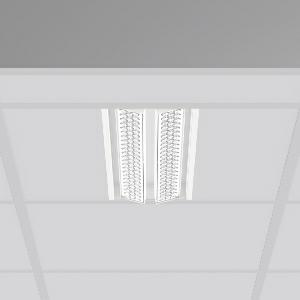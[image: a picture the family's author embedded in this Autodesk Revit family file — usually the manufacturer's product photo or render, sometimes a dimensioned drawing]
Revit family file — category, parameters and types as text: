
# Revit family: tx-move_901734_002_3_e3f6
name_source: partatom
category: Lighting Fixtures
units: mm (PartAtom-declared; Revit-internal decimal feet)

## family parameters
Cut with Voids When Loaded = No
Host = Face
Light Source = No
Part Type = Normal
Room Calculation Point = No
Round Connector Dimension = Use Diameter
Shared = No

## types (1)
- MultiLumen 1 (1 x LED Modul 835, 2650 lm, 3500)
    Apparent Load = 35 VA
    CIE Flux Codes = 65 90 98 100 100
    Color Rendering = 80
    Color Temperature = 3500
    Default Elevation = 1800 mm
    Description = Series: TX-MOVE
Einlege/Einbau-Flächenstrahler. Housing: sheet steel, powder-coated. 2xSwivel range: 90°. High-efficiency LED units with optimum light control thanks to clear plastic (PC) lens optics. Spezielle Mikrostrukturen reduzieren Gelbsaum. Asymmetrical light distribution. Suitable for laying in grid ceiling module 600. Connected converter included in separate gearbox.Suitable for through-wiring.MultiLumen: Luminous flux adjustable in 3 steps. Accessories: Mounting frame for installation in suspended ceilings. Environmentally friendly and resource-saving due to replaceable and recyclable components. 
Colour: traffic white, matt (RAL 9016)
Length: 597 mm
Width: 190 mm
Height: 39 mm
Cut-out length: 577.5 mm
Cut-out width: 174 mm
Recess height: 100 mm
Lamp: LED
Socket: without socket
Colour temperature: 3500K
Colour rendering index (CRI): 80
System power: 35 W
Rated luminous flux: 5300 lm
Luminous efficiency: 151 lm/W
System power 2: 47 W
Rated luminous flux 2: 6900 lm
Luminous efficiency 2: 147 lm/W
System power 3: 68 W
Rated luminous flux 3: 9450 lm
Luminous efficiency 3: 139 lm/W
Control gear: Regulated power supply
Protection class: I
Type of protection: IP 20
    Height = 0 mm  [stored 0 ft]
    Lamp = 1 x LED Modul 835
    Lamp Light Flux = 2650 lm
    Lamp count = 1
    Length = 597 mm
    Lifetime = 50000 h
    Luminous efficacy = 151 lm/W
    Manufacturer = RZB
    ModVariant = No
    Model = 901734.002.3
    Mounting Place = Ceiling, Wall
    Mounting Type = Recessed
    Number of Poles = 1
    OnlyDefault = Yes
    Power Factor = 1
    Product Name = TX-MOVE
    Product group = Recessed projectors
    ProductGroupID = 401
    Protection Class = Protection class I
    Protection Degree = IP 20
    RLX_Detail_Level = 1
    RLX_Emergency_Light_Flux = 0 lm
    RLX_Emergency_Type = 0
    RLX_Emergency_Type_DB = No
    RlxData = <blob elided: 56205 chars, md5=05e01e32>
    Socket = socket
    Standby Power = 0 W
    System Light Flux = 5300 lm
    System Power = 35 W
    Type Comments = MultiLumen 1
    Type Image = 901733.002.jpg
    URL = http://relux.com
    VarID = multilumen_1
    Voltage = 230 V
    Voltage Range = 220-240 V
    Weight = 0.00 kg
    Width = 190 mm  [stored 0.62336 ft]

note: [stored X ft] marks values corroborated as IEEE doubles in the binary element streams (Revit-internal decimal feet)

## geometry (parser evidence)
native form markers: Blend x4, Sweep x14
no freeform markers — native parametric forms only
